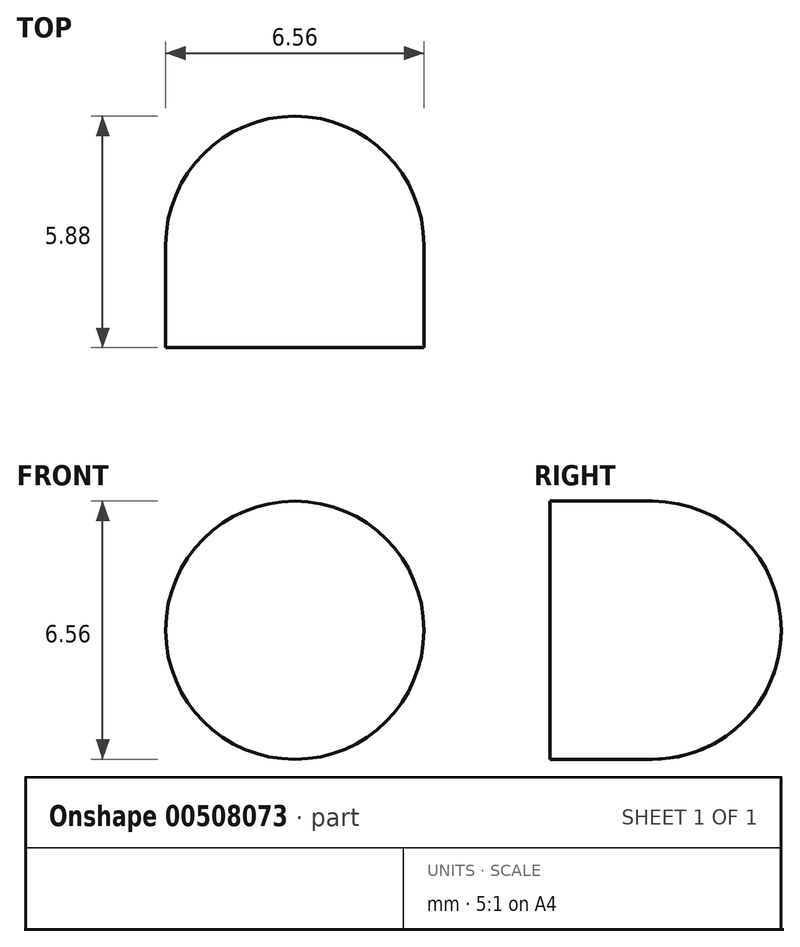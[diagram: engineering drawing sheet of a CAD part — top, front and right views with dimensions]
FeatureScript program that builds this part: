
annotation { "Feature Type Name" : "Feature", "Feature Type Description" : "" }
export const myFeature = defineFeature(function(context is Context, id is Id, definition is map)
    precondition{}
    {
        {
            var Q0;
            Q0=qCreatedBy(makeId("Front.planeOp"),FACE);
            var sketch = newSketch(context, id + "F0", { "sketchPlane" : qUnion([Q0])});
            skCircle(sketch, "E0", {"center": v(0, 0) * mm, "radius": 3.28 * mm});
            skSolve(sketch);
        }
        {
            var Q0;
            Q0 = qSketchRegion(id + "F0", true);
            extrude(context, id + "F1", {"entities" : qUnion([Q0]), "depth" : 5.88 * mm, "offsetDistance" : 25 * mm});
        }
        {
            var Q0;
            Q0=makeQuery(id+"F1.opExtrude","CAP_EDGE",EDGE,{"disambiguationData":[OSD([sQuery(id+"F0.wireOp",EDGE,"E0")])],"isStart":true});
            fillet(context, id + "F2", {"entities" : qUnion([Q0]), "radius" : 3.28 * mm, "tangentPropagation" : true, "allowEdgeOverflow" : false});
        }
    });
